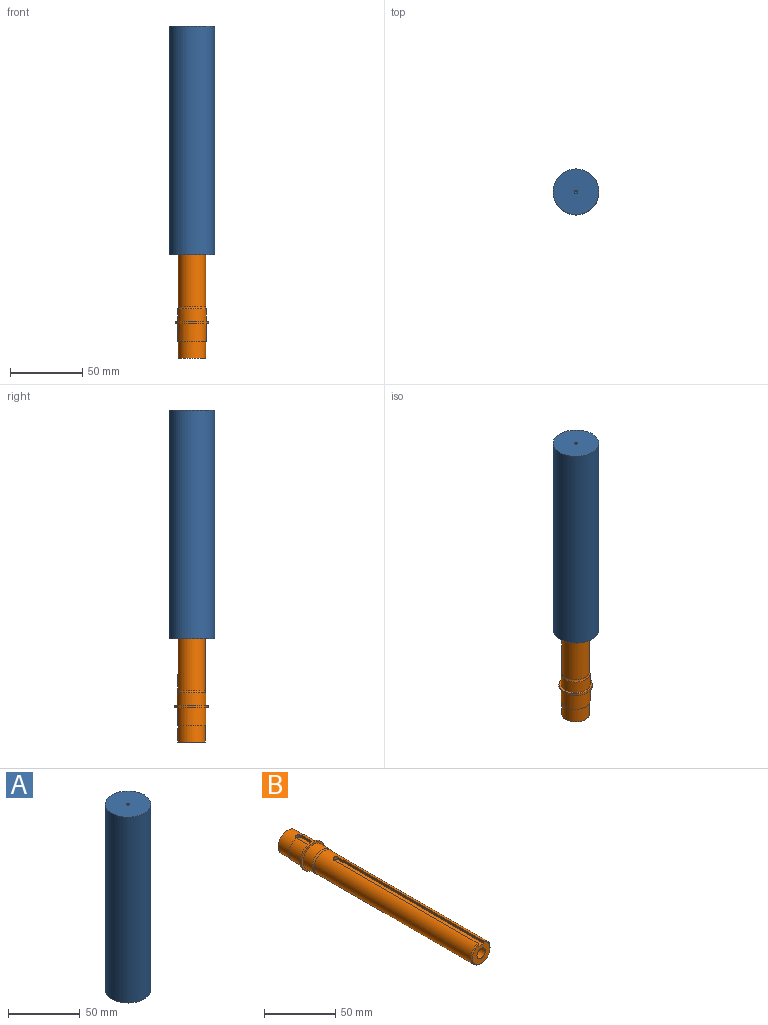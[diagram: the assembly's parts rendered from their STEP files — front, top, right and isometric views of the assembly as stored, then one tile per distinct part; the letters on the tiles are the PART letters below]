
ASSEMBLY  parts=2 mates=1
PART A: 10 faces, bbox 31.8x31.8x158.8 mm
  f0: plane 31.75x31.75mm, normal (0,0,-1), area 497mm2, adj f1,f2,f3,f4,f5
  f1: cylinder r=9.53mm len=120.65mm, axis (0,0,-1), area 6638.2mm2, adj f0,f4,f5,f6
  f2: cylinder r=15.88mm len=158.75mm, axis (0,0,-1), area 15834.6mm2, adj f0,f7
  f3: plane 120.65x4.78mm, normal (0,-1,0), area 576.1mm2, adj f0,f4,f5,f6
  f4: plane 120.65x2.24mm, normal (-1,0,0), area 269.7mm2, adj f0,f1,f3,f6
  f5: plane 120.65x2.24mm, normal (1,0,0), area 269.7mm2, adj f0,f1,f3,f6
  f6: plane 20.98x19.05mm, normal (0,0,-1), area 294.7mm2, adj f1,f3,f4,f5
  f7: plane 31.75x31.75mm, normal (0,0,1), area 787.3mm2, adj f2,f9
  f8: cone r=0mm half-angle=59deg, axis (0,0,1), area 5.2mm2, adj f9
  f9: cylinder r=1.19mm len=19.05mm, axis (0,0,1), area 142.5mm2, adj f7,f8
PART B: 23 faces, bbox 23.2x192.4x23.2 mm
  f0: cylinder r=10mm len=20mm, axis (0,1,0), area 560.5mm2, adj f3,f10
  f1: cylinder r=9.53mm len=155.65mm, axis (0,1,0), area 8618.2mm2, adj f3,f4,f5,f6,f22
  f2: plane 17.46x17.13mm, normal (0,-1,0), area 176.6mm2, adj f5,f6,f7,f21,f22
  f3: torus R=12.7mm, axis (0,1,0), area 107mm2, adj f0,f1
  f4: cylinder r=2.38mm len=4.76mm, axis (0,0,1), area 16.7mm2, adj f1,f5,f6,f7
  f5: plane 143.75x2.09mm, normal (-1,0,0), area 298.5mm2, adj f1,f2,f4,f7,f22
  f6: plane 143.75x2.09mm, normal (1,0,0), area 298.5mm2, adj f1,f2,f4,f7,f22
  f7: plane 146.13x4.76mm, normal (0,0,1), area 693.5mm2, adj f2,f4,f5,f6
  f8: plane 23.18x23.18mm, normal (0,1,0), area 107.7mm2, adj f9,f19
  f9: cylinder r=11.59mm len=23.18mm, axis (0,1,0), area 115.6mm2, adj f8,f10
  f10: plane 23.18x23.18mm, normal (0,-1,0), area 107.7mm2, adj f0,f9
  f11: plane 19.05x19.05mm, normal (0,1,0), area 285mm2, adj f12
  f12: cylinder r=9.53mm len=19.05mm, axis (0,1,0), area 656.1mm2, adj f11,f13,f16
  f13: cylinder r=2.38mm len=4.76mm, axis (0,0,1), area 13.1mm2, adj f12,f14,f15,f17
  f14: plane 15.08x4.76mm, normal (0,0,1), area 67mm2, adj f13,f15,f17,f18
  f15: plane 10.32x2.09mm, normal (-1,0,0), area 21.6mm2, adj f13,f14,f16,f18,f19
  f16: plane 20x19.71mm, normal (0,1,0), area 26.9mm2, adj f12,f15,f17,f19
  f17: plane 10.32x2.09mm, normal (1,0,0), area 21.6mm2, adj f13,f14,f16,f18,f19
  f18: cylinder r=2.38mm len=4.76mm, axis (0,0,1), area 16.7mm2, adj f14,f15,f17,f19
  f19: cylinder r=10mm len=20mm, axis (0,1,0), area 739.4mm2, adj f8,f15,f16,f17,f18
  f20: cone r=4.22mm half-angle=59deg, axis (0,-1,0), area 65.2mm2, adj f21
  f21: cylinder r=4.22mm len=25.4mm, axis (0,-1,0), area 672.9mm2, adj f2,f20
  f22: cone r=8.73mm half-angle=45deg, axis (0,1,0), area 59mm2, adj f1,f2,f5,f6
PLACE A at identity
PLACE B rot(axis=(-1,0,0),90deg) t=(0,0.34,-71.79)mm
MATE fastened B.f0 <-> A.f6  axis (0,0,1) through (0,0.34,120.65)mm
